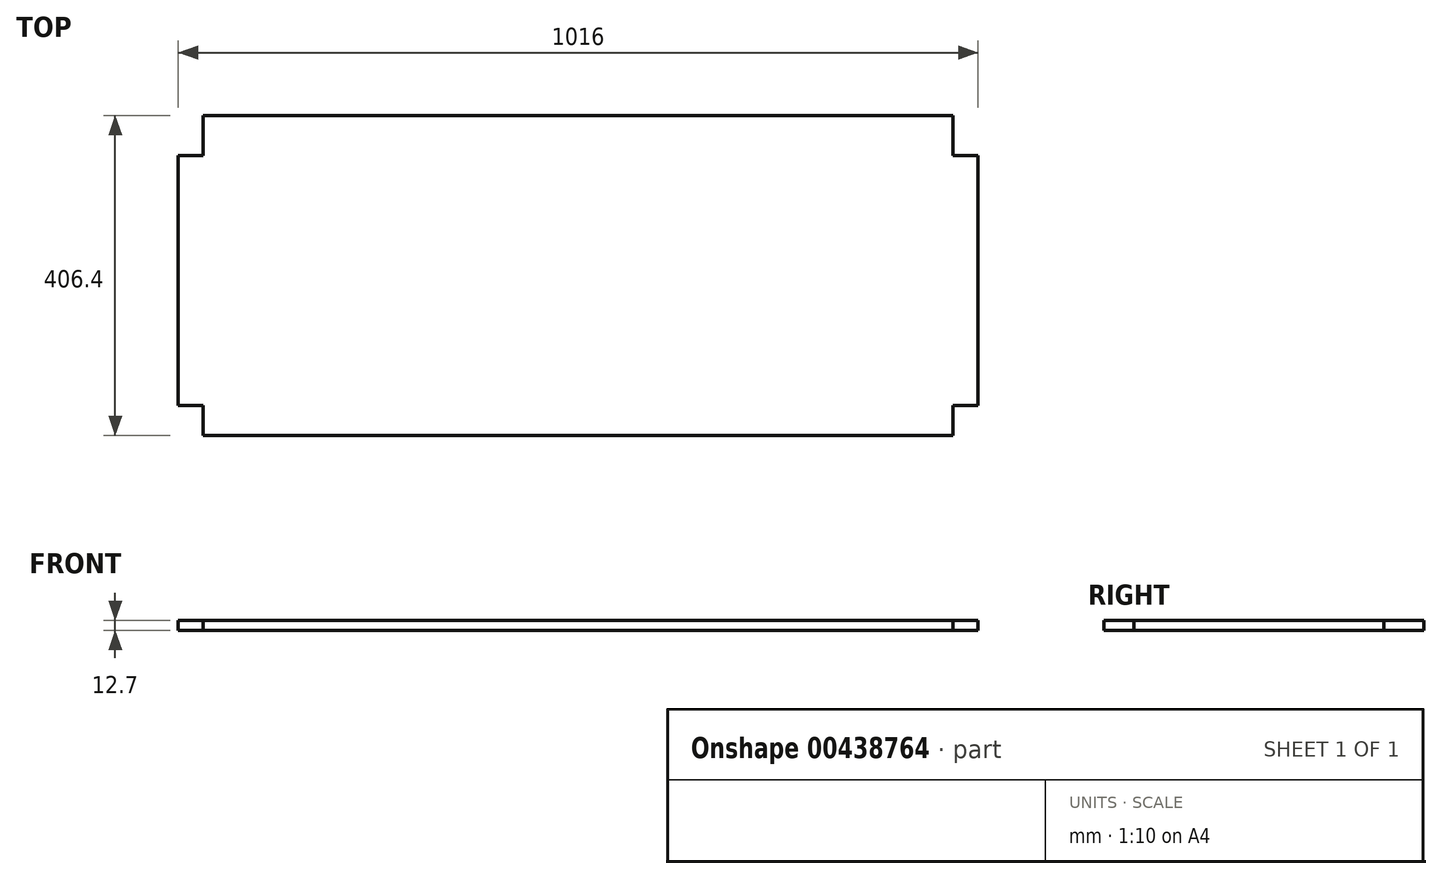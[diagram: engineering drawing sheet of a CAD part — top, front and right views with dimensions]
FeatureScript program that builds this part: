
annotation { "Feature Type Name" : "Feature", "Feature Type Description" : "" }
export const myFeature = defineFeature(function(context is Context, id is Id, definition is map)
    precondition{}
    {
        {
            var Q0;
            Q0=qCreatedBy(makeId("Top.planeOp"),FACE);
            var sketch = newSketch(context, id + "F0", { "sketchPlane" : qUnion([Q0])});
            skLineSegment(sketch, "E0.bottom", {"start": v(508, -203.2) * mm, "end": v(-508, -203.2) * mm});
            skLineSegment(sketch, "E0.top", {"start": v(508, 203.2) * mm, "end": v(-508, 203.2) * mm});
            skLineSegment(sketch, "E0.left", {"start": v(508, -203.2) * mm, "end": v(508, 203.2) * mm});
            skLineSegment(sketch, "E0.right", {"start": v(-508, -203.2) * mm, "end": v(-508, 203.2) * mm});
            skPoint(sketch, "E0.middle", {"position": v(0, 0) * mm});
            skLineSegment(sketch, "E1", {"start": v(-508, 152.4) * mm, "end": v(-476.25, 152.4) * mm});
            skLineSegment(sketch, "E2", {"start": v(-476.25, 152.4) * mm, "end": v(-476.25, 203.2) * mm});
            skLineSegment(sketch, "E3", {"start": v(476.25, 203.2) * mm, "end": v(476.25, 152.4) * mm});
            skLineSegment(sketch, "E4", {"start": v(476.25, 152.4) * mm, "end": v(508, 152.4) * mm});
            skLineSegment(sketch, "E5", {"start": v(-508, -165.1) * mm, "end": v(-476.25, -165.1) * mm});
            skLineSegment(sketch, "E6", {"start": v(-476.25, -165.1) * mm, "end": v(-476.25, -203.2) * mm});
            skLineSegment(sketch, "E7", {"start": v(508, -165.1) * mm, "end": v(476.25, -165.1) * mm});
            skLineSegment(sketch, "E8", {"start": v(476.25, -165.1) * mm, "end": v(476.25, -203.2) * mm});
            skSolve(sketch);
        }
        {
            var Q0;
            {var subQ4=sQuery(id+"F0.wireOp",EDGE,"E1");Q0=makeQuery(id+"F0.imprint","IMPRINT",FACE,{"disambiguationData":[TD([[makeQuery(id+"F0.imprint","IMPRINT",EDGE,{"derivedFrom":subQ4}),-1.0]])]});}
            extrude(context, id + "F1", {"entities" : qUnion([Q0]), "depth" : 12.7 * mm});
        }
    });
